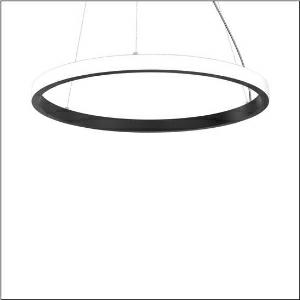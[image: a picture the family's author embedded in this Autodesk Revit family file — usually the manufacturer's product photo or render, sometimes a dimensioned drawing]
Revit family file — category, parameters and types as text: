
# Revit family: silica_21_ring-o_5pjbo4d1104a
name_source: partatom
category: Lighting Fixtures
units: mm (PartAtom-declared; Revit-internal decimal feet)

## family parameters
Cut with Voids When Loaded = No
Host = Face
Light Source = No
Part Type = Normal
Room Calculation Point = No
Round Connector Dimension = Use Diameter
Shared = No

## types (1)
- Silica 21 Ring-O (1 x LED, 8820 lm, 140 W, 3000K)
    Apparent Load = 140 VA
    CIE Flux Codes = 2 16 49 50 100
    Color Rendering = 80
    Color Temperature = 3000K
    Default Elevation = 1800 mm
    Description = Silica 21 Ring-O, suspended luminaire, of PMMA, frosted, light emission: outer ring side luminous distribution, primary light characteristic: symmetric, installation type: suspended mounting, LED, rated luminous flux: 8.820lm, luminous efficacy: 63lm/W, light colour: 830, colour temperature: 3000K, control gear: DALI 2, with terminal, 5-pole, mains connection: 230V, AC/DC, 0/50..60Hz, rated input power: 140W, housing, of extruded aluminium section, jet black (RAL 9005), diameter: 1.480mm, ceiling canopy, jet black (RAL 9005), protection rating (lamp compartment): IP40, insulation class (complete): insulation class I (protective earthing), certification: CE, impact resistance: IK02, permissible operating ambient temperature: 0..+35°C, packaging unit: 1 piece
    Height = 48 mm  [stored 0.15748 ft]
    Lamp = 1 x LED
    Lamp Light Flux = 8820 lm
    Lamp Power = 140 W
    Lamp count = 1
    Length = 1480 mm
    Luminous efficacy = 63 lm/W
    Manufacturer = Siteco
    ModVariant = No
    Model = 5PJBO4D1104A
    Mounting Place = Ceiling
    Mounting Type = Pendant
    Number of Poles = 1
    OnlyDefault = Yes
    Power Factor = 1
    Product Name = Silica 21 Ring-O
    Product group = suspended luminaire
    ProductGroupID = 904
    Protection Class = Protection class I
    Protection Degree = IP 40
    RLX_Detail_Level = 1
    RLX_Emergency_Light_Flux = 0 lm
    RLX_Emergency_Type = 0
    RLX_Emergency_Type_DB = No
    RlxData = <blob elided: 20545 chars, md5=1a797da3>
    Socket = socket
    Standby Power = 0 W
    System Light Flux = 8820 lm
    System Power = 140 W
    Type Comments = Product without accessories
    Type Image = l_1258389.jpg
    URL = http://relux.com
    VarID = ---
    Voltage = 0 V
    Weight = 0.00 kg
    Width = 0 mm  [stored 0 ft]

note: [stored X ft] marks values corroborated as IEEE doubles in the binary element streams (Revit-internal decimal feet)

## geometry (parser evidence)
native form markers: Blend x4, Sweep x14
no freeform markers — native parametric forms only
